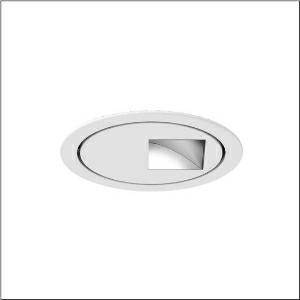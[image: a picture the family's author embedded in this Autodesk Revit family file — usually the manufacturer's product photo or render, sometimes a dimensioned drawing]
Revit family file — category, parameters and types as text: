
# Revit family: lunis_11_mini_round_51dk11b72wm21
name_source: partatom
category: Lighting Fixtures
units: mm (PartAtom-declared; Revit-internal decimal feet)

## family parameters
Cut with Voids When Loaded = No
Host = Face
Light Source = No
Part Type = Normal
Room Calculation Point = No
Round Connector Dimension = Use Diameter
Shared = No

## types (1)
- Lunis 11 mini round (1 x LED 3000K / CRI = 90 (unbekannt), 1930 lm, 3000K)
    Apparent Load = 28 VA
    CIE Flux Codes = 44 77 97 100 100
    Color Rendering = 90
    Color Temperature = 3000K
    Default Elevation = 1800 mm
    Description = Lunis 11 mini round, downlight, light control with wallwasher, of highly reflective aluminium, highly specular, light emission: direct distribution, LED rated luminous flux: 1.930lm, light colour: 930, control gear: ECG, with terminal, 3-pole, mains connection: 220..230V, AC/DC, 0/50..60Hz, LED module, luminaire module, of aluminium, highly specular, white, diameter: 176mm, clamping range: 1..40mm, recessing ring, of plastic, traffic white (RAL 9016), protection rating (complete): IP20, insulation class (complete): insulation class II (safety insulation), certification: CE, permissible ambient temperature for indoor applications: 0..+35°C, packaging unit: 1 piece
    Height = 0 mm  [stored 0 ft]
    Lamp = 1 x LED 3000K / CRI >= 90 (unbekannt)
    Lamp Light Flux = 1930 lm
    Lamp count = 1
    Length = 176 mm
    Luminous efficacy = 69 lm/W
    Manufacturer = Siteco
    ModVariant = No
    Model = 51DK11B72WM21
    Mounting Place = Ceiling
    Mounting Type = Recessed
    Number of Poles = 1
    OnlyDefault = Yes
    Power Factor = 1
    Product Name = Lunis 11 mini round
    Product group = downlight
    ProductGroupID = 401
    Protection Class = Protection class II
    Protection Degree = IP 20
    RLX_Detail_Level = 1
    RLX_Emergency_Light_Flux = 0 lm
    RLX_Emergency_Type = 0
    RLX_Emergency_Type_DB = No
    RlxData = <blob elided: 59401 chars, md5=4a002e15>
    Socket = socket
    Standby Power = 0 W
    System Light Flux = 1930 lm
    System Power = 28 W
    Type Comments = Product without accessories
    Type Image = l_1004772.jpg
    URL = http://relux.com
    VarID = ---
    Voltage = 0 V
    Weight = 0.00 kg
    Width = 176 mm

note: [stored X ft] marks values corroborated as IEEE doubles in the binary element streams (Revit-internal decimal feet)

## geometry (parser evidence)
native form markers: Blend x4, Sweep x11
no freeform markers — native parametric forms only
